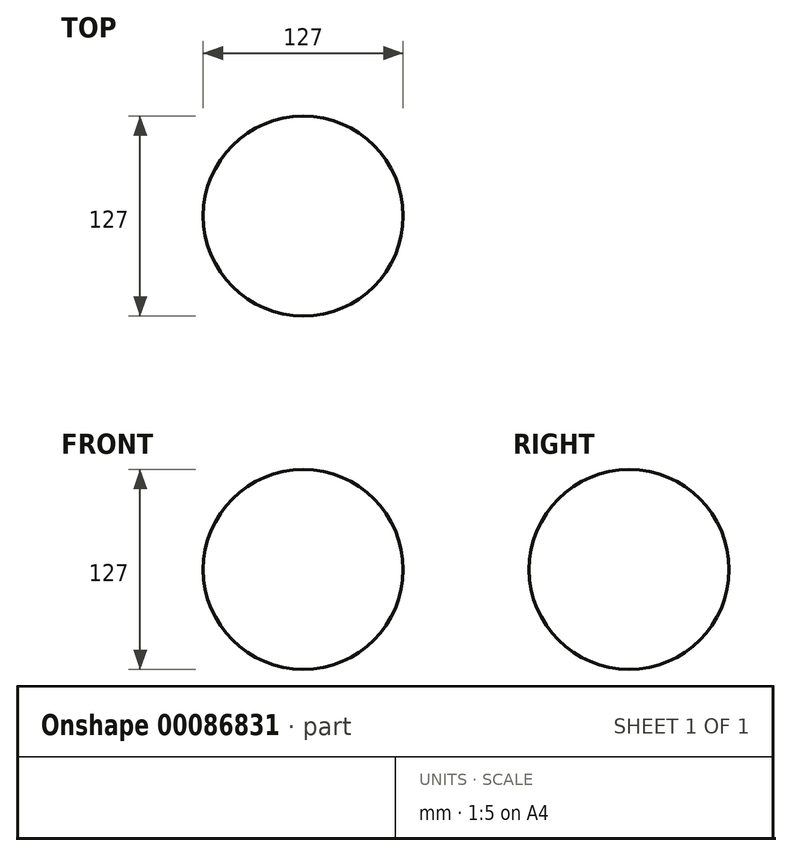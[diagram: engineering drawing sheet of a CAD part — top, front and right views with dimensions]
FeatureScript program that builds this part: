
annotation { "Feature Type Name" : "Feature", "Feature Type Description" : "" }
export const myFeature = defineFeature(function(context is Context, id is Id, definition is map)
    precondition{}
    {
        {
            var Q0;
            Q0=qCreatedBy(makeId("Front.planeOp"),FACE);
            var sketch = newSketch(context, id + "F0", { "sketchPlane" : qUnion([Q0])});
            skArc(sketch, "E0", {"start": v(0, -63.5) * mm, "mid": v(63.5, 0) * mm, "end": v(0, 63.5) * mm});
            skLineSegment(sketch, "E1", {"start": v(0, 63.5) * mm, "end": v(0, -63.5) * mm, "construction": true});
            skLineSegment(sketch, "E2", {"start": v(0, 63.5) * mm, "end": v(0, -63.5) * mm});
            skSolve(sketch);
        }
        {
            var Q0;
            Q0=qCreatedBy(makeId("Front.planeOp"),FACE);
            var sketch = newSketch(context, id + "F1", { "sketchPlane" : qUnion([Q0])});
            skLineSegment(sketch, "E3", {"start": v(0, 76.62) * mm, "end": v(0, -76.03) * mm, "construction": true});
            skSolve(sketch);
        }
        {
            var Q0;
            Q0=qSketchRegion(id+"F1",true);
            var Q1;
            Q1=makeQuery(id+"F0.imprint","IMPRINT",FACE,{"disambiguationData":[TD([[makeQuery(id+"F0.imprint","IMPRINT",EDGE,{"derivedFrom":sQuery(id+"F0.wireOp",EDGE,"E0")}),1.0]])]});
            var Q2;
            Q2=sQuery(id+"F1.wireOp",EDGE,"E3");
            revolve(context, id + "F2", {"entities" : qUnion([Q0, Q1]), "axis" : qUnion([Q2]), "revolveType" : RevolveType.FULL});
        }
    });
